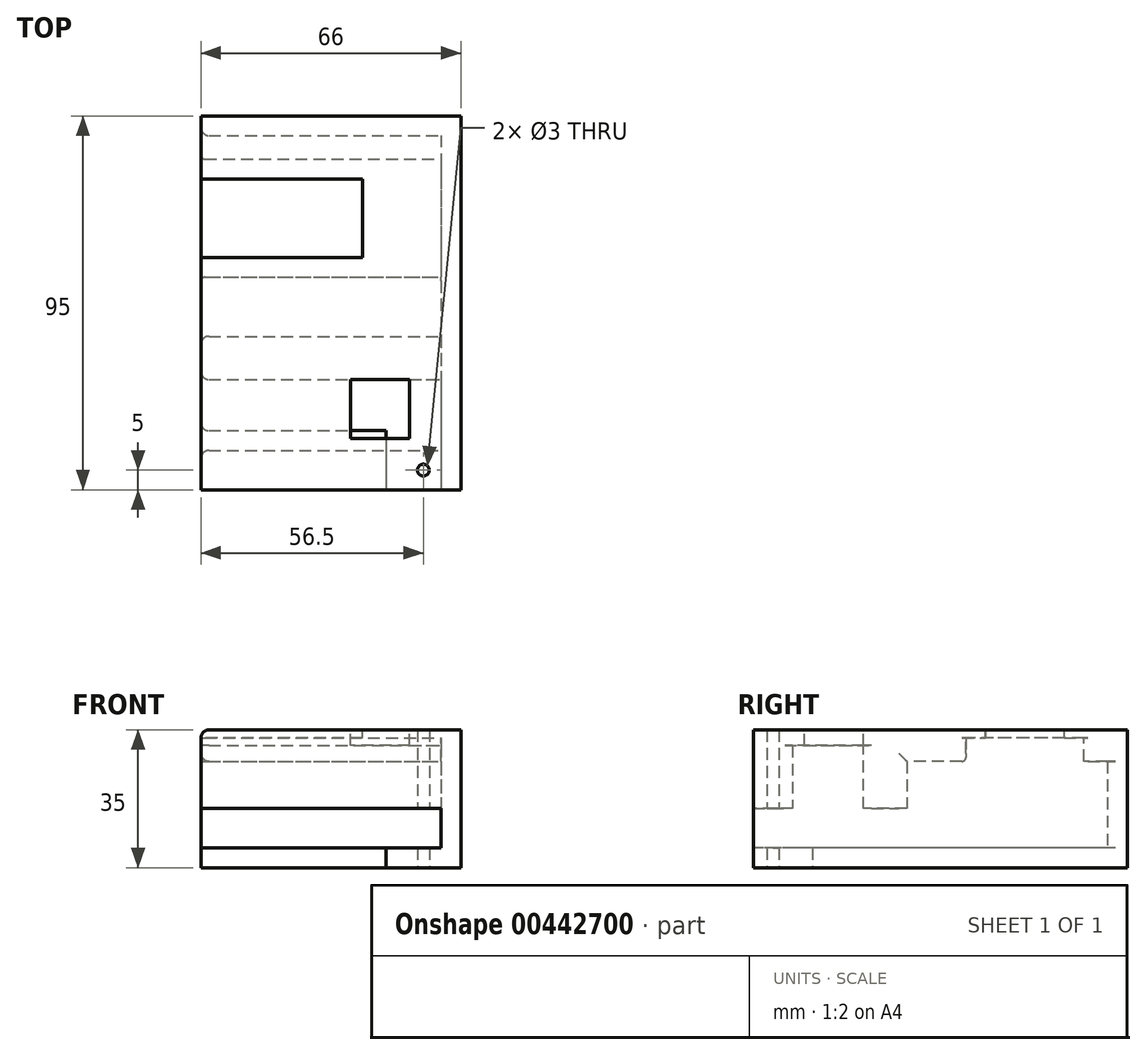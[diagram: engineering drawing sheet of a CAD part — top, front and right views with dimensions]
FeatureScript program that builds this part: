
annotation { "Feature Type Name" : "Feature", "Feature Type Description" : "" }
export const myFeature = defineFeature(function(context is Context, id is Id, definition is map)
    precondition{}
    {
        {
            var Q0;
            Q0=qCreatedBy(makeId("Top.planeOp"),FACE);
            var sketch = newSketch(context, id + "F0", { "sketchPlane" : qUnion([Q0])});
            skLineSegment(sketch, "E0.bottom", {"start": v(-33, 47.5) * mm, "end": v(33, 47.5) * mm});
            skLineSegment(sketch, "E0.top", {"start": v(14, -47.5) * mm, "end": v(33, -47.5) * mm});
            skLineSegment(sketch, "E0.left", {"start": v(-33, 47.5) * mm, "end": v(-33, -32.5) * mm});
            skLineSegment(sketch, "E0.right", {"start": v(33, 47.5) * mm, "end": v(33, -47.5) * mm});
            skPoint(sketch, "E0.middle", {"position": v(0, 0) * mm});
            skLineSegment(sketch, "E1", {"start": v(-33, -32.5) * mm, "end": v(14, -32.5) * mm});
            skLineSegment(sketch, "E2", {"start": v(14, -32.5) * mm, "end": v(14, -47.5) * mm});
            skPoint(sketch, "E3.orphan", {"position": v(-33, -47.5) * mm});
            skSolve(sketch);
        }
        {
            var Q0;
            Q0 = qSketchRegion(id + "F0", true);
            extrude(context, id + "F1", {"entities" : qUnion([Q0]), "depth" : 5 * mm});
        }
        {
            var Q0;
            Q0=makeQuery(id+"F1.opExtrude","CAP_FACE",FACE,{"disambiguationData":[OSD([sQuery(id+"F0.wireOp",EDGE,"E0.bottom"),sQuery(id+"F0.wireOp",EDGE,"E0.top"),sQuery(id+"F0.wireOp",EDGE,"E0.left"),sQuery(id+"F0.wireOp",EDGE,"E0.right"),sQuery(id+"F0.wireOp",EDGE,"E1"),sQuery(id+"F0.wireOp",EDGE,"E2")])],"isStart":false});
            var sketch = newSketch(context, id + "F2", { "sketchPlane" : qUnion([Q0])});
            skLineSegment(sketch, "E4.0", {"start": v(28, 42.5) * mm, "end": v(28, -47.5) * mm});
            skLineSegment(sketch, "E4.1", {"start": v(-33, 42.5) * mm, "end": v(28, 42.5) * mm});
            skLineSegment(sketch, "E5", {"start": v(-33, 42.5) * mm, "end": v(-33, 47.5) * mm});
            skLineSegment(sketch, "E6", {"start": v(28, -47.5) * mm, "end": v(33, -47.5) * mm});
            skLineSegment(sketch, "E7.0", {"start": v(-33, 47.5) * mm, "end": v(33, 47.5) * mm});
            skLineSegment(sketch, "E7.1", {"start": v(33, 47.5) * mm, "end": v(33, -47.5) * mm});
            skSolve(sketch);
        }
        {
            var Q0;
            Q0 = qSketchRegion(id + "F2", true);
            extrude(context, id + "F3", {"entities" : qUnion([Q0]), "operationType" : NewBodyOperationType.ADD, "depth" : 30 * mm});
        }
        {
            var Q0;
            Q0=makeQuery(id+"F3.opExtrude","SWEPT_FACE",FACE,{"disambiguationData":[OSD([sQuery(id+"F2.wireOp",EDGE,"E4.0")])]});
            var sketch = newSketch(context, id + "F4", { "sketchPlane" : qUnion([Q0])});
            skLineSegment(sketch, "E8.0", {"start": v(-42.5, 35) * mm, "end": v(47.5, 35) * mm});
            skLineSegment(sketch, "E9", {"start": v(-42.5, 33) * mm, "end": v(47.5, 33) * mm, "construction": true});
            skLineSegment(sketch, "E10", {"start": v(-42.5, 27) * mm, "end": v(47.5, 27) * mm, "construction": true});
            skLineSegment(sketch, "E11", {"start": v(-42.5, 15) * mm, "end": v(47.5, 15) * mm, "construction": true});
            skLineSegment(sketch, "E12", {"start": v(-42.5, 35) * mm, "end": v(-42.5, 27) * mm});
            skLineSegment(sketch, "E13", {"start": v(-36.5, 27) * mm, "end": v(-36.5, 33) * mm});
            skLineSegment(sketch, "E14", {"start": v(-36.5, 33) * mm, "end": v(-6.5, 33) * mm});
            skLineSegment(sketch, "E15", {"start": v(-6.5, 33) * mm, "end": v(-6.5, 27) * mm});
            skLineSegment(sketch, "E16", {"start": v(-6.5, 27) * mm, "end": v(8.5, 27) * mm});
            skLineSegment(sketch, "E17", {"start": v(8.5, 27) * mm, "end": v(8.5, 15) * mm});
            skLineSegment(sketch, "E18", {"start": v(8.5, 15) * mm, "end": v(19.5, 15) * mm});
            skLineSegment(sketch, "E19", {"start": v(19.5, 15) * mm, "end": v(19.5, 31) * mm});
            skPoint(sketch, "E20.endSnap0", {"position": v(2.5, 27) * mm});
            skLineSegment(sketch, "E21", {"start": v(37.5, 15) * mm, "end": v(47.5, 15) * mm});
            skLineSegment(sketch, "E22", {"start": v(19.5, 31) * mm, "end": v(37.5, 31) * mm});
            skLineSegment(sketch, "E23", {"start": v(37.5, 31) * mm, "end": v(37.5, 15) * mm});
            skLineSegment(sketch, "E24", {"start": v(47.5, 15) * mm, "end": v(47.5, 35) * mm});
            skLineSegment(sketch, "E25", {"start": v(-42.5, 27) * mm, "end": v(-36.5, 27) * mm});
            skLineSegment(sketch, "E26", {"start": v(47.5, 35) * mm, "end": v(-42.5, 35) * mm});
            skSolve(sketch);
        }
        {
            var Q0;
            Q0 = qSketchRegion(id + "F4", true);
            var Q1;
            Q1=makeQuery(id+"F3.boolean.opBoolean","MERGE",FACE,{"derivedFrom":[makeQuery(id+"F1.opExtrude","SWEPT_FACE",FACE,{"disambiguationData":[OSD([sQuery(id+"F0.wireOp",EDGE,"E0.left")])]}),makeQuery(id+"F3.opExtrude","SWEPT_FACE",FACE,{"disambiguationData":[OSD([sQuery(id+"F2.wireOp",EDGE,"E5")])]})]});
            extrude(context, id + "F5", {"entities" : qUnion([Q0]), "operationType" : NewBodyOperationType.ADD, "endBound" : BoundingType.UP_TO_SURFACE, "endBoundEntityFace" : qUnion([Q1]), "depth" : 25 * mm});
        }
        {
            var Q0;
            Q0=makeQuery(id+"F5.boolean.opBoolean","MERGE",FACE,{"derivedFrom":[makeQuery(id+"F3.opExtrude","CAP_FACE",FACE,{"disambiguationData":[OSD([sQuery(id+"F2.wireOp",EDGE,"E4.0"),sQuery(id+"F2.wireOp",EDGE,"E4.1"),sQuery(id+"F2.wireOp",EDGE,"E5"),sQuery(id+"F2.wireOp",EDGE,"E6"),sQuery(id+"F2.wireOp",EDGE,"E7.0"),sQuery(id+"F2.wireOp",EDGE,"E7.1")])],"isStart":false}),makeQuery(id+"F5.opExtrude","SWEPT_FACE",FACE,{"disambiguationData":[OSD([sQuery(id+"F4.wireOp",EDGE,"E26")])]})]});
            var sketch = newSketch(context, id + "F6", { "sketchPlane" : qUnion([Q0])});
            skLineSegment(sketch, "E27", {"start": v(-33, 11.5) * mm, "end": v(8, 11.5) * mm});
            skLineSegment(sketch, "E28", {"start": v(8, 11.5) * mm, "end": v(8, 31.5) * mm});
            skLineSegment(sketch, "E29", {"start": v(8, 31.5) * mm, "end": v(-33, 31.5) * mm});
            skLineSegment(sketch, "E30", {"start": v(-33, 31.5) * mm, "end": v(-33, 11.5) * mm});
            skLineSegment(sketch, "E31.bottom", {"start": v(5, -19.5) * mm, "end": v(20, -19.5) * mm});
            skLineSegment(sketch, "E31.top", {"start": v(5, -34.5) * mm, "end": v(20, -34.5) * mm});
            skLineSegment(sketch, "E31.left", {"start": v(5, -19.5) * mm, "end": v(5, -34.5) * mm});
            skLineSegment(sketch, "E31.right", {"start": v(20, -19.5) * mm, "end": v(20, -34.5) * mm});
            skPoint(sketch, "E31.middle", {"position": v(12.5, -27) * mm});
            skSolve(sketch);
        }
        {
            var Q0;
            Q0 = qSketchRegion(id + "F6", true);
            extrude(context, id + "F7", {"entities" : qUnion([Q0]), "operationType" : NewBodyOperationType.REMOVE, "endBound" : BoundingType.UP_TO_NEXT, "oppositeDirection" : true, "depth" : 25 * mm});
        }
        {
            var Q0;
            Q0=makeQuery(id+"F1.opExtrude","CAP_FACE",FACE,{"disambiguationData":[OSD([sQuery(id+"F0.wireOp",EDGE,"E0.bottom"),sQuery(id+"F0.wireOp",EDGE,"E0.top"),sQuery(id+"F0.wireOp",EDGE,"E0.left"),sQuery(id+"F0.wireOp",EDGE,"E0.right"),sQuery(id+"F0.wireOp",EDGE,"E1"),sQuery(id+"F0.wireOp",EDGE,"E2")])],"isStart":true});
            var sketch = newSketch(context, id + "F8", { "sketchPlane" : qUnion([Q0])});
            skCircle(sketch, "E32", {"center": v(23.5, 42.5) * mm, "radius": 1.5 * mm});
            skPoint(sketch, "E32.centerSnap0", {"position": v(23.5, 47.5) * mm});
            skSolve(sketch);
        }
        {
            var Q0;
            Q0 = qSketchRegion(id + "F8", true);
            extrude(context, id + "F9", {"entities" : qUnion([Q0]), "operationType" : NewBodyOperationType.REMOVE, "endBound" : BoundingType.THROUGH_ALL, "oppositeDirection" : true, "depth" : 25 * mm});
        }
        {
            var Q0;
            {var subQ0=sQuery(id+"F2.wireOp",EDGE,"E5");var subQ2=sQuery(id+"F4.wireOp",EDGE,"E26");Q0=makeQuery(id+"F7.boolean.opBoolean","SPLIT",EDGE,{"disambiguationData":[TD([makeQuery(id+"F1.opExtrude","SWEPT_FACE",FACE,{"disambiguationData":[OSD([sQuery(id+"F0.wireOp",EDGE,"E0.top")])]})])],"derivedFrom":makeQuery(id+"F5.boolean.opBoolean","MERGE",EDGE,{"derivedFrom":[makeQuery(id+"F3.opExtrude","CAP_EDGE",EDGE,{"disambiguationData":[OSD([subQ0])],"isStart":false}),makeQuery(id+"F5.opExtrude","CAP_EDGE",EDGE,{"disambiguationData":[OSD([subQ2])],"isStart":false})]})});}
            var Q1;
            {var subQ0=sQuery(id+"F2.wireOp",EDGE,"E5");var subQ2=sQuery(id+"F4.wireOp",EDGE,"E26");Q1=makeQuery(id+"F7.boolean.opBoolean","SPLIT",EDGE,{"disambiguationData":[TD([makeQuery(id+"F1.opExtrude","SWEPT_FACE",FACE,{"disambiguationData":[OSD([sQuery(id+"F0.wireOp",EDGE,"E0.bottom")])]})])],"derivedFrom":makeQuery(id+"F5.boolean.opBoolean","MERGE",EDGE,{"derivedFrom":[makeQuery(id+"F3.opExtrude","CAP_EDGE",EDGE,{"disambiguationData":[OSD([subQ0])],"isStart":false}),makeQuery(id+"F5.opExtrude","CAP_EDGE",EDGE,{"disambiguationData":[OSD([subQ2])],"isStart":false})]})});}
            var Q2;
            Q2=makeQuery(id+"F5.opExtrude","CAP_EDGE",EDGE,{"disambiguationData":[OSD([sQuery(id+"F4.wireOp",EDGE,"E19")])],"isStart":false});
            var Q3;
            Q3=makeQuery(id+"F5.opExtrude","CAP_EDGE",EDGE,{"disambiguationData":[OSD([sQuery(id+"F4.wireOp",EDGE,"E23")])],"isStart":false});
            var Q4;
            Q4=makeQuery(id+"F5.opExtrude","CAP_EDGE",EDGE,{"disambiguationData":[OSD([sQuery(id+"F4.wireOp",EDGE,"E17")])],"isStart":false});
            var Q5;
            Q5=makeQuery(id+"F5.opExtrude","CAP_EDGE",EDGE,{"disambiguationData":[OSD([sQuery(id+"F4.wireOp",EDGE,"E16")])],"isStart":false});
            var Q6;
            Q6=makeQuery(id+"F3.opExtrude","SWEPT_EDGE",EDGE,{"disambiguationData":[OSD([sQuery(id+"F0.wireOp",EDGE,"E0.left"),sQuery(id+"F2.wireOp",EDGE,"E4.1"),sQuery(id+"F2.wireOp",EDGE,"E5")])]});
            var Q7;
            Q7=makeQuery(id+"F1.opExtrude","SWEPT_EDGE",EDGE,{"disambiguationData":[OSD([sQuery(id+"F0.wireOp",EDGE,"E0.left"),sQuery(id+"F0.wireOp",EDGE,"E1")])]});
            fillet(context, id + "F10", {"entities" : qUnion([Q0, Q1, Q2, Q3, Q4, Q5, Q6, Q7]), "radius" : 2 * mm, "tangentPropagation" : true, "allowEdgeOverflow" : false});
        }
        {
            var Q0;
            Q0=makeQuery(id+"F5.opExtrude","CAP_EDGE",EDGE,{"disambiguationData":[OSD([sQuery(id+"F4.wireOp",EDGE,"E13")])],"isStart":false});
            var Q1;
            Q1=makeQuery(id+"F5.opExtrude","CAP_EDGE",EDGE,{"disambiguationData":[OSD([sQuery(id+"F4.wireOp",EDGE,"E15")])],"isStart":false});
            fillet(context, id + "F11", {"entities" : qUnion([Q0, Q1]), "radius" : 1 * mm, "tangentPropagation" : true, "allowEdgeOverflow" : false});
        }
    });
